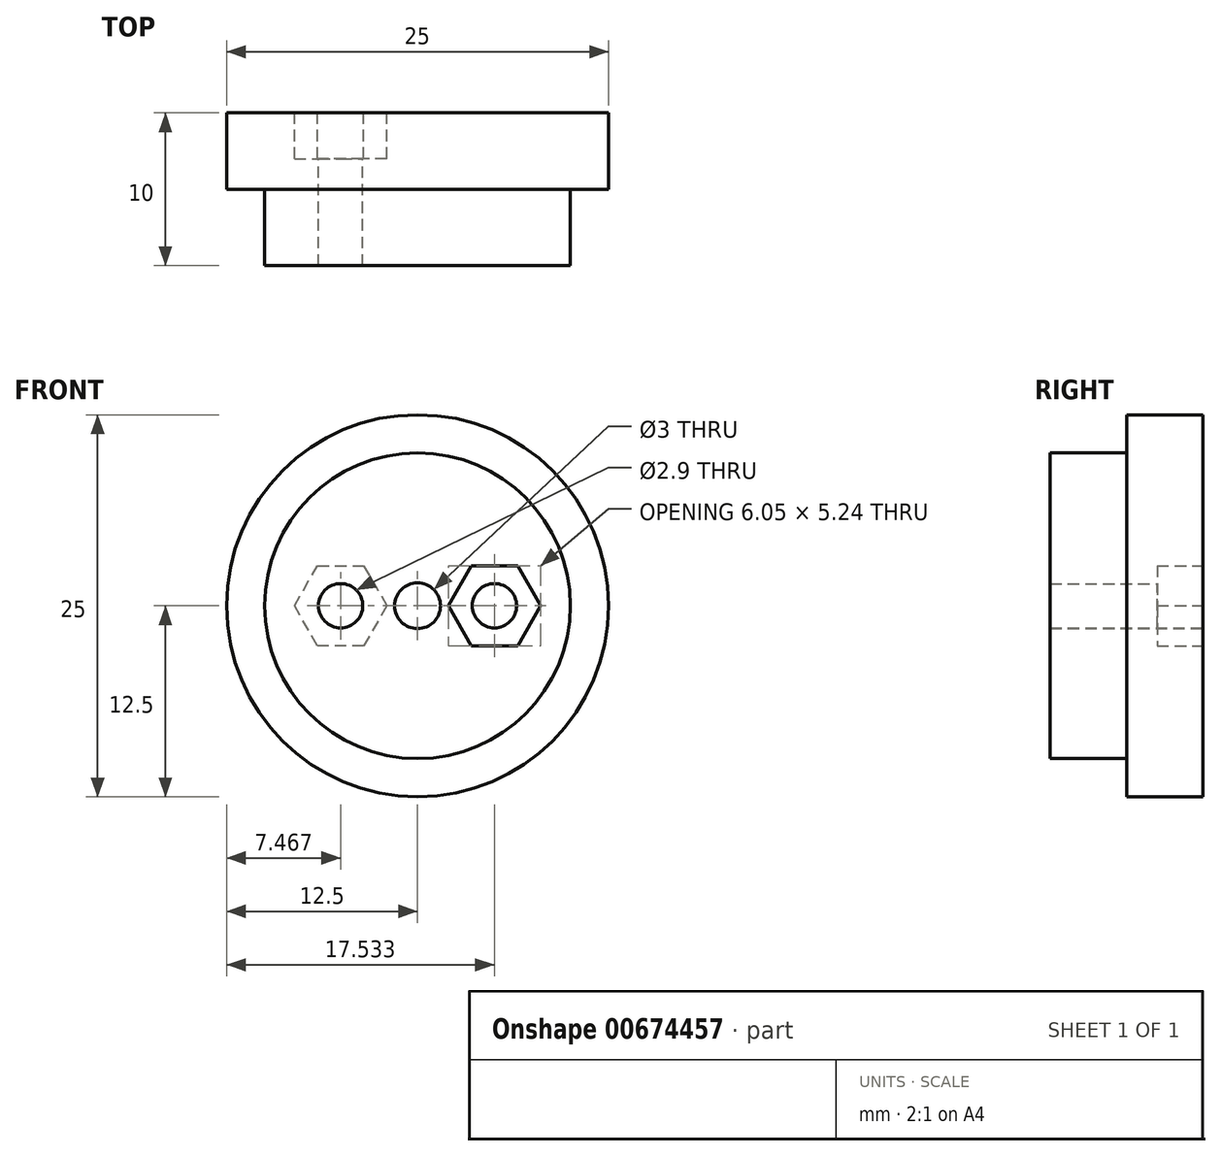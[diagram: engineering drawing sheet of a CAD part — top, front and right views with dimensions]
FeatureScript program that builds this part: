
annotation { "Feature Type Name" : "Feature", "Feature Type Description" : "" }
export const myFeature = defineFeature(function(context is Context, id is Id, definition is map)
    precondition{}
    {
        {
            var Q0;
            Q0=qCreatedBy(makeId("Front.planeOp"),FACE);
            var sketch = newSketch(context, id + "F0", { "sketchPlane" : qUnion([Q0])});
            skCircle(sketch, "E0", {"center": v(0, 0) * mm, "radius": 1.5 * mm});
            skCircle(sketch, "E1", {"center": v(0, 0) * mm, "radius": 10 * mm});
            skCircle(sketch, "E2", {"center": v(0, 0) * mm, "radius": 12.5 * mm});
            skSolve(sketch);
        }
        {
            var Q0;
            Q0=makeQuery(id+"F0.imprint","IMPRINT",FACE,{"disambiguationData":[TD([[makeQuery(id+"F0.imprint","IMPRINT",EDGE,{"derivedFrom":sQuery(id+"F0.wireOp",EDGE,"E1")}),-1.0]])]});
            extrude(context, id + "F1", {"entities" : qUnion([Q0]), "depth" : 5 * mm, "offsetDistance" : 25 * mm});
        }
        {
            var Q0;
            Q0=makeQuery(id+"F0.imprint","IMPRINT",FACE,{"disambiguationData":[TD([[makeQuery(id+"F0.imprint","IMPRINT",EDGE,{"derivedFrom":sQuery(id+"F0.wireOp",EDGE,"E0")}),-1.0]])]});
            extrude(context, id + "F2", {"entities" : qUnion([Q0]), "operationType" : NewBodyOperationType.ADD, "depth" : 10 * mm, "offsetDistance" : 25 * mm});
        }
        {
            var Q0;
            Q0=qCreatedBy(makeId("Front.planeOp"),FACE);
            var sketch = newSketch(context, id + "F3", { "sketchPlane" : qUnion([Q0])});
            skCircle(sketch, "E3.cCircle", {"center": v(-5.03, 0) * mm, "radius": 2.62 * mm, "construction": true});
            skLineSegment(sketch, "E3.0", {"start": v(-3.52, -2.62) * mm, "end": v(-6.55, -2.62) * mm});
            skLineSegment(sketch, "E3.1", {"start": v(-6.55, -2.62) * mm, "end": v(-8.06, 0) * mm});
            skLineSegment(sketch, "E3.2", {"start": v(-8.06, 0) * mm, "end": v(-6.55, 2.62) * mm});
            skLineSegment(sketch, "E3.3", {"start": v(-6.55, 2.62) * mm, "end": v(-3.52, 2.62) * mm});
            skLineSegment(sketch, "E3.4", {"start": v(-3.52, 2.62) * mm, "end": v(-2, 0) * mm});
            skLineSegment(sketch, "E3.5", {"start": v(-2, 0) * mm, "end": v(-3.52, -2.62) * mm});
            skPoint(sketch, "E3.0.midPoint", {"position": v(-5.03, -2.62) * mm});
            skCircle(sketch, "E4.MirrorC", {"center": v(5.03, 0) * mm, "radius": 2.62 * mm, "construction": true});
            skLineSegment(sketch, "E5.MirrorCS", {"start": v(8.06, 0) * mm, "end": v(6.55, 2.62) * mm});
            skLineSegment(sketch, "E6.MirrorCS", {"start": v(6.55, 2.62) * mm, "end": v(3.52, 2.62) * mm});
            skLineSegment(sketch, "E7.MirrorCS", {"start": v(3.52, 2.62) * mm, "end": v(2, 0) * mm});
            skLineSegment(sketch, "E8.MirrorCS", {"start": v(2, 0) * mm, "end": v(3.52, -2.62) * mm});
            skLineSegment(sketch, "E9.MirrorCS", {"start": v(3.52, -2.62) * mm, "end": v(6.55, -2.62) * mm});
            skLineSegment(sketch, "E10.MirrorCS", {"start": v(6.55, -2.62) * mm, "end": v(8.06, 0) * mm});
            skCircle(sketch, "E11", {"center": v(-5.03, 0) * mm, "radius": 1.45 * mm});
            skCircle(sketch, "E12.MirrorC", {"center": v(5.03, 0) * mm, "radius": 1.45 * mm});
            skSolve(sketch);
        }
        {
            var Q0;
            Q0=makeQuery(id+"F3.imprint","IMPRINT",FACE,{"disambiguationData":[TD([[makeQuery(id+"F3.imprint","IMPRINT",EDGE,{"derivedFrom":sQuery(id+"F3.wireOp",EDGE,"E11")}),1.0]])]});
            extrude(context, id + "F4", {"entities" : qUnion([Q0]), "operationType" : NewBodyOperationType.REMOVE, "depth" : 25 * mm, "offsetDistance" : 25 * mm});
        }
        {
            var Q0;
            Q0=makeQuery(id+"F3.imprint","IMPRINT",FACE,{"disambiguationData":[TD([[makeQuery(id+"F3.imprint","IMPRINT",EDGE,{"derivedFrom":sQuery(id+"F3.wireOp",EDGE,"E12.MirrorC")}),-1.0]])]});
            extrude(context, id + "F5", {"entities" : qUnion([Q0]), "operationType" : NewBodyOperationType.REMOVE, "depth" : 25 * mm, "offsetDistance" : 25 * mm});
        }
        {
            var Q0;
            Q0=makeQuery(id+"F3.imprint","IMPRINT",FACE,{"disambiguationData":[TD([[makeQuery(id+"F3.imprint","IMPRINT",EDGE,{"derivedFrom":sQuery(id+"F3.wireOp",EDGE,"E3.0")}),-1.0]])]});
            var Q1;
            Q1=makeQuery(id+"F3.imprint","IMPRINT",FACE,{"disambiguationData":[TD([[makeQuery(id+"F3.imprint","IMPRINT",EDGE,{"derivedFrom":sQuery(id+"F3.wireOp",EDGE,"E5.MirrorCS")}),1.0]])]});
            extrude(context, id + "F6", {"entities" : qUnion([Q0, Q1]), "operationType" : NewBodyOperationType.REMOVE, "depth" : 3 * mm, "offsetDistance" : 25 * mm});
        }
    });
